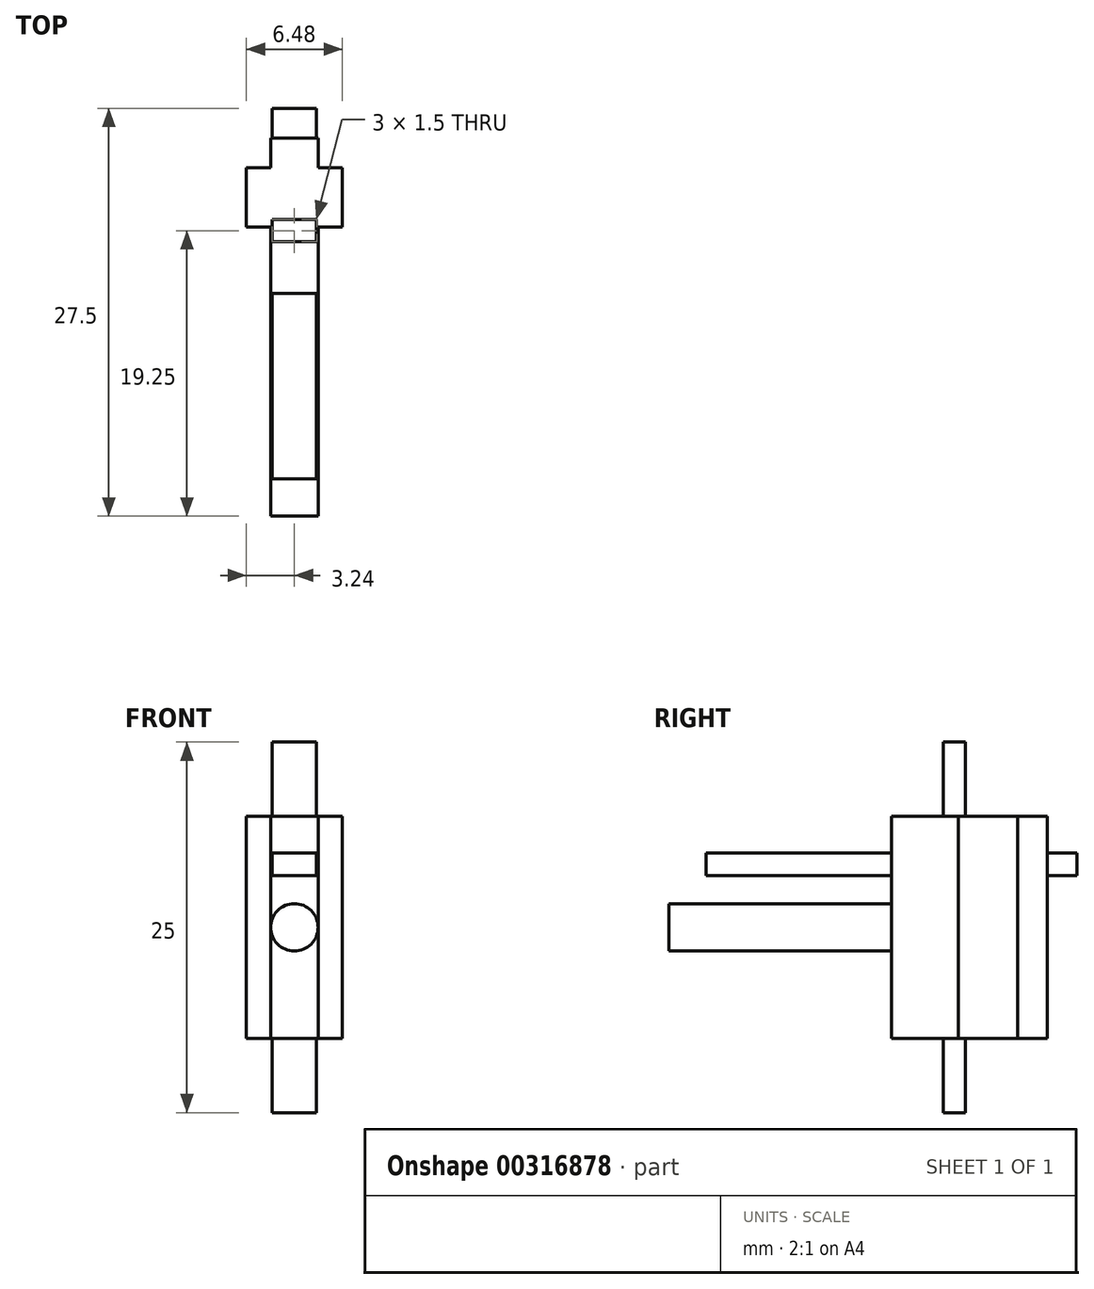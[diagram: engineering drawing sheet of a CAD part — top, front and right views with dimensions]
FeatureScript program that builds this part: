
annotation { "Feature Type Name" : "Feature", "Feature Type Description" : "" }
export const myFeature = defineFeature(function(context is Context, id is Id, definition is map)
    precondition{}
    {
        {
            var Q0;
            Q0=qCreatedBy(makeId("Top.planeOp"),FACE);
            var sketch = newSketch(context, id + "F0", { "sketchPlane" : qUnion([Q0])});
            skLineSegment(sketch, "E0", {"start": v(0, 0) * mm, "end": v(0, 10.5) * mm, "construction": true});
            skLineSegment(sketch, "E1", {"start": v(0, 10.5) * mm, "end": v(-1.6, 10.5) * mm});
            skLineSegment(sketch, "E2", {"start": v(-1.6, 10.5) * mm, "end": v(-1.6, 8.5) * mm});
            skLineSegment(sketch, "E3", {"start": v(-1.6, 8.5) * mm, "end": v(-3.24, 8.5) * mm});
            skLineSegment(sketch, "E4", {"start": v(-3.24, 8.5) * mm, "end": v(-3.24, 4.5) * mm});
            skLineSegment(sketch, "E5", {"start": v(-3.24, 4.5) * mm, "end": v(-1.6, 4.5) * mm});
            skLineSegment(sketch, "E6", {"start": v(-1.6, 4.5) * mm, "end": v(-1.6, 0) * mm});
            skLineSegment(sketch, "E7", {"start": v(-1.6, 0) * mm, "end": v(0, 0) * mm});
            skLineSegment(sketch, "E8.MirrorCS", {"start": v(0, 10.5) * mm, "end": v(1.6, 10.5) * mm});
            skLineSegment(sketch, "E9.MirrorCS", {"start": v(1.6, 10.5) * mm, "end": v(1.6, 8.5) * mm});
            skLineSegment(sketch, "E10.MirrorCS", {"start": v(3.24, 4.5) * mm, "end": v(1.6, 4.5) * mm});
            skLineSegment(sketch, "E11.MirrorCS", {"start": v(1.6, 4.5) * mm, "end": v(1.6, 0) * mm});
            skLineSegment(sketch, "E12.MirrorCS", {"start": v(3.24, 8.5) * mm, "end": v(3.24, 4.5) * mm});
            skLineSegment(sketch, "E13.MirrorCS", {"start": v(1.6, 0) * mm, "end": v(0, 0) * mm});
            skLineSegment(sketch, "E14.MirrorCS", {"start": v(1.6, 8.5) * mm, "end": v(3.24, 8.5) * mm});
            skSolve(sketch);
        }
        {
            var Q0;
            Q0=makeQuery(id+"F0.imprint","IMPRINT",FACE,{"disambiguationData":[TD([[makeQuery(id+"F0.imprint","IMPRINT",EDGE,{"derivedFrom":sQuery(id+"F0.wireOp",EDGE,"E1")}),1.0]])]});
            extrude(context, id + "F1", {"entities" : qUnion([Q0]), "endBound" : BoundingType.SYMMETRIC, "oppositeDirection" : true, "depth" : 15 * mm});
        }
        {
            var Q0;
            Q0=qCreatedBy(makeId("Front.planeOp"),FACE);
            var sketch = newSketch(context, id + "F2", { "sketchPlane" : qUnion([Q0])});
            skCircle(sketch, "E15", {"center": v(0, 0) * mm, "radius": 1.6 * mm});
            skSolve(sketch);
        }
        {
            var Q0;
            Q0=makeQuery(id+"F2.imprint","IMPRINT",FACE,{"disambiguationData":[TD([[makeQuery(id+"F2.imprint","IMPRINT",EDGE,{"derivedFrom":sQuery(id+"F2.wireOp",EDGE,"E15")}),1.0]])]});
            extrude(context, id + "F3", {"entities" : qUnion([Q0]), "operationType" : NewBodyOperationType.ADD, "depth" : 15 * mm});
        }
        {
            var Q0;
            Q0=qCreatedBy(makeId("Front.planeOp"),FACE);
            var sketch = newSketch(context, id + "F4", { "sketchPlane" : qUnion([Q0])});
            skLineSegment(sketch, "E16.bottom", {"start": v(1.5, 3.5) * mm, "end": v(-1.5, 3.5) * mm});
            skLineSegment(sketch, "E16.top", {"start": v(1.5, 5) * mm, "end": v(-1.5, 5) * mm});
            skLineSegment(sketch, "E16.left", {"start": v(1.5, 3.5) * mm, "end": v(1.5, 5) * mm});
            skLineSegment(sketch, "E16.right", {"start": v(-1.5, 3.5) * mm, "end": v(-1.5, 5) * mm});
            skPoint(sketch, "E16.middle", {"position": v(0, 4.25) * mm});
            skSolve(sketch);
        }
        {
            var Q0;
            Q0 = qSketchRegion(id + "F4", true);
            extrude(context, id + "F5", {"entities" : qUnion([Q0]), "endBound" : BoundingType.SYMMETRIC, "depth" : 25 * mm});
        }
        {
            var Q0;
            Q0=qCreatedBy(makeId("Top.planeOp"),FACE);
            var sketch = newSketch(context, id + "F6", { "sketchPlane" : qUnion([Q0])});
            skLineSegment(sketch, "E17.bottom", {"start": v(1.5, 3.5) * mm, "end": v(-1.5, 3.5) * mm});
            skLineSegment(sketch, "E17.top", {"start": v(1.5, 5) * mm, "end": v(-1.5, 5) * mm});
            skLineSegment(sketch, "E17.left", {"start": v(1.5, 3.5) * mm, "end": v(1.5, 5) * mm});
            skLineSegment(sketch, "E17.right", {"start": v(-1.5, 3.5) * mm, "end": v(-1.5, 5) * mm});
            skPoint(sketch, "E17.middle", {"position": v(0, 4.25) * mm});
            skSolve(sketch);
        }
        {
            var Q0;
            Q0 = qSketchRegion(id + "F6", true);
            extrude(context, id + "F7", {"entities" : qUnion([Q0]), "operationType" : NewBodyOperationType.ADD, "endBound" : BoundingType.SYMMETRIC, "depth" : 25 * mm});
        }
    });
